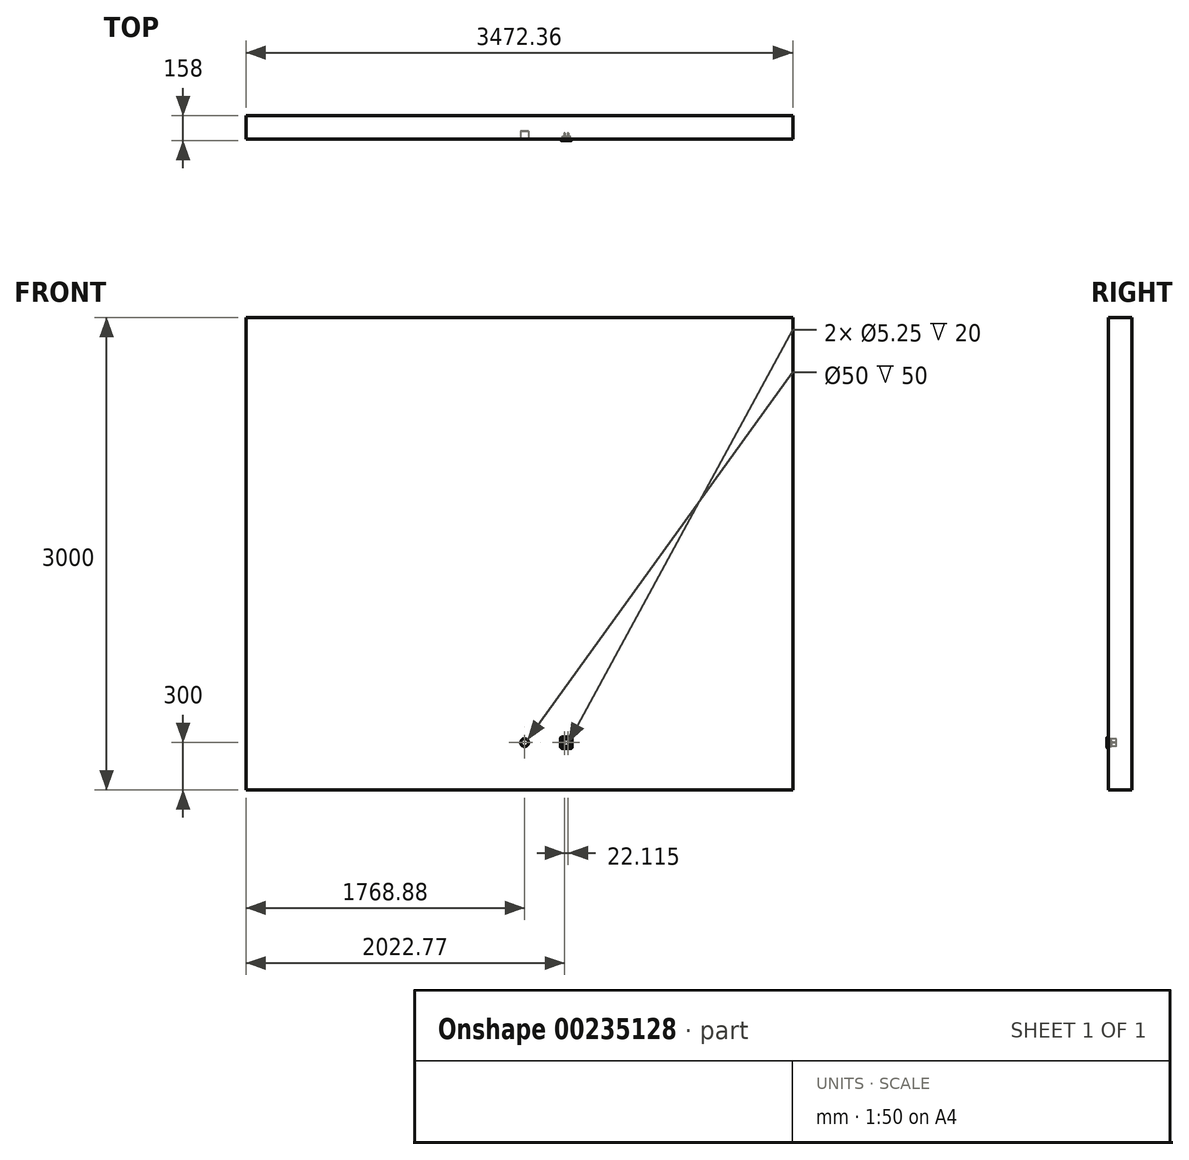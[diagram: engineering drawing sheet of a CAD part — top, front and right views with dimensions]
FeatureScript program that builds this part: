
annotation { "Feature Type Name" : "Feature", "Feature Type Description" : "" }
export const myFeature = defineFeature(function(context is Context, id is Id, definition is map)
    precondition{}
    {
        {
            var Q0;
            Q0=qCreatedBy(makeId("Front.planeOp"),FACE);
            var sketch = newSketch(context, id + "F0", { "sketchPlane" : qUnion([Q0])});
            skLineSegment(sketch, "E0.bottom", {"start": v(0, 0) * mm, "end": v(3472.36, 0) * mm});
            skLineSegment(sketch, "E0.top", {"start": v(0, 3000) * mm, "end": v(3472.36, 3000) * mm});
            skLineSegment(sketch, "E0.left", {"start": v(0, 0) * mm, "end": v(0, 3000) * mm});
            skLineSegment(sketch, "E0.right", {"start": v(3472.36, 0) * mm, "end": v(3472.36, 3000) * mm});
            skSolve(sketch);
        }
        {
            var Q0;
            Q0=makeQuery(id+"F0.imprint","IMPRINT",FACE,{"disambiguationData":[TD([[makeQuery(id+"F0.imprint","IMPRINT",EDGE,{"derivedFrom":sQuery(id+"F0.wireOp",EDGE,"E0.bottom")}),1.0]])]});
            extrude(context, id + "F1", {"entities" : qUnion([Q0]), "depth" : 150 * mm});
        }
        {
            var Q0;
            Q0=makeQuery(id+"F1.opExtrude","CAP_FACE",FACE,{"disambiguationData":[OSD([sQuery(id+"F0.wireOp",EDGE,"E0.bottom"),sQuery(id+"F0.wireOp",EDGE,"E0.top"),sQuery(id+"F0.wireOp",EDGE,"E0.left"),sQuery(id+"F0.wireOp",EDGE,"E0.right")])],"isStart":false});
            var sketch = newSketch(context, id + "F2", { "sketchPlane" : qUnion([Q0])});
            skCircle(sketch, "E1", {"center": v(1768.88, 300) * mm, "radius": 25 * mm});
            skCircle(sketch, "E2", {"center": v(1768.88, 300) * mm, "radius": 24.95 * mm});
            skSolve(sketch);
        }
        {
            var Q0;
            Q0=makeQuery(id+"F2.imprint","IMPRINT",FACE,{"disambiguationData":[TD([[makeQuery(id+"F2.imprint","IMPRINT",EDGE,{"derivedFrom":sQuery(id+"F2.wireOp",EDGE,"E1")}),1.0]])]});
            extrude(context, id + "F3", {"entities" : qUnion([Q0]), "operationType" : NewBodyOperationType.REMOVE, "oppositeDirection" : true, "depth" : 50 * mm});
        }
        {
            var Q0;
            {var subQ0=sQuery(id+"F0.wireOp",EDGE,"E0.right");var subQ1=sQuery(id+"F0.wireOp",EDGE,"E0.left");var subQ2=sQuery(id+"F0.wireOp",EDGE,"E0.top");var subQ3=sQuery(id+"F0.wireOp",EDGE,"E0.bottom");Q0=makeQuery(id+"F3.boolean.opBoolean","SPLIT",FACE,{"disambiguationData":[TD([makeQuery(id+"F1.opExtrude","SWEPT_FACE",FACE,{"disambiguationData":[OSD([subQ3])]})])],"derivedFrom":makeQuery(id+"F1.opExtrude","CAP_FACE",FACE,{"disambiguationData":[OSD([subQ3,subQ2,subQ1,subQ0])],"isStart":false})});}
            var sketch = newSketch(context, id + "F4", { "sketchPlane" : qUnion([Q0])});
            skArc(sketch, "E3", {"start": v(2010.84, 290.18) * mm, "mid": v(2033.83, 275) * mm, "end": v(2056.82, 290.18) * mm});
            skLineSegment(sketch, "E4.bottom", {"start": v(2071.28, 337.45) * mm, "end": v(1996.38, 337.45) * mm});
            skLineSegment(sketch, "E4.top", {"start": v(2071.28, 262.55) * mm, "end": v(1996.38, 262.55) * mm});
            skLineSegment(sketch, "E4.left", {"start": v(2071.28, 337.45) * mm, "end": v(2071.28, 262.55) * mm});
            skLineSegment(sketch, "E4.right", {"start": v(1996.38, 337.45) * mm, "end": v(1996.38, 262.55) * mm});
            skCircle(sketch, "E5", {"center": v(2022.77, 300) * mm, "radius": 2.63 * mm});
            skLineSegment(sketch, "E6", {"start": v(2033.83, 300) * mm, "end": v(2033.83, 328.03) * mm});
            skCircle(sketch, "E7.MirrorC", {"center": v(2044.88, 300) * mm, "radius": 2.63 * mm});
            skLineSegment(sketch, "E8", {"start": v(2010.84, 309.82) * mm, "end": v(2010.84, 302.5) * mm});
            skLineSegment(sketch, "E9", {"start": v(2010.84, 302.5) * mm, "end": v(2008.95, 302.5) * mm});
            skLineSegment(sketch, "E10", {"start": v(2008.95, 302.5) * mm, "end": v(2008.95, 297.5) * mm});
            skLineSegment(sketch, "E11", {"start": v(2008.95, 297.5) * mm, "end": v(2010.84, 297.5) * mm});
            skLineSegment(sketch, "E12", {"start": v(2010.84, 297.5) * mm, "end": v(2010.84, 290.18) * mm});
            skLineSegment(sketch, "E13.MirrorCS", {"start": v(2056.82, 309.82) * mm, "end": v(2056.82, 302.5) * mm});
            skLineSegment(sketch, "E14.MirrorCS", {"start": v(2056.82, 302.5) * mm, "end": v(2058.7, 302.5) * mm});
            skLineSegment(sketch, "E15.MirrorCS", {"start": v(2058.7, 302.5) * mm, "end": v(2058.7, 297.5) * mm});
            skLineSegment(sketch, "E16.MirrorCS", {"start": v(2058.7, 297.5) * mm, "end": v(2056.82, 297.5) * mm});
            skLineSegment(sketch, "E17.MirrorCS", {"start": v(2056.82, 297.5) * mm, "end": v(2056.82, 290.18) * mm});
            skArc(sketch, "E18.trimOffspring", {"start": v(2056.82, 309.82) * mm, "mid": v(2033.83, 325) * mm, "end": v(2010.84, 309.82) * mm});
            skSolve(sketch);
        }
        {
            var Q0;
            Q0 = qSketchRegion(id + "F4", true);
            var Q1;
            Q1=makeQuery(id+"F4.imprint","IMPRINT",FACE,{"disambiguationData":[TD([[makeQuery(id+"F4.imprint","IMPRINT",EDGE,{"derivedFrom":sQuery(id+"F4.wireOp",EDGE,"E4.bottom")}),1.0]])]});
            extrude(context, id + "F5", {"entities" : qUnion([Q0, Q1]), "operationType" : NewBodyOperationType.ADD, "depth" : 8 * mm});
        }
        {
            var Q0;
            Q0=makeQuery(id+"F5.opExtrude","SWEPT_EDGE",EDGE,{"disambiguationData":[OSD([sQuery(id+"F4.wireOp",EDGE,"E4.bottom"),sQuery(id+"F4.wireOp",EDGE,"E4.right")])]});
            var Q1;
            Q1=makeQuery(id+"F5.opExtrude","SWEPT_EDGE",EDGE,{"disambiguationData":[OSD([sQuery(id+"F4.wireOp",EDGE,"E4.top"),sQuery(id+"F4.wireOp",EDGE,"E4.right")])]});
            var Q2;
            Q2=makeQuery(id+"F5.opExtrude","SWEPT_EDGE",EDGE,{"disambiguationData":[OSD([sQuery(id+"F4.wireOp",EDGE,"E4.top"),sQuery(id+"F4.wireOp",EDGE,"E4.left")])]});
            var Q3;
            Q3=makeQuery(id+"F5.opExtrude","SWEPT_EDGE",EDGE,{"disambiguationData":[OSD([sQuery(id+"F4.wireOp",EDGE,"E4.bottom"),sQuery(id+"F4.wireOp",EDGE,"E4.left")])]});
            fillet(context, id + "F6", {"entities" : qUnion([Q0, Q1, Q2, Q3]), "radius" : 13 * mm, "tangentPropagation" : true, "allowEdgeOverflow" : false});
        }
        {
            var Q0;
            {var subQ0=sQuery(id+"F4.wireOp",EDGE,"E4.right");var subQ1=sQuery(id+"F4.wireOp",EDGE,"E4.bottom");Q0=makeQuery(id+"F6.opFillet","BLEND_EDGE",EDGE,{"blendedFrom":[makeQuery(id+"F5.opExtrude","SWEPT_EDGE",EDGE,{"disambiguationData":[OSD([subQ1,subQ0])]}),makeQuery(id+"F5.opExtrude","CAP_FACE",FACE,{"disambiguationData":[OSD([sQuery(id+"F4.wireOp",EDGE,"E3"),subQ1,sQuery(id+"F4.wireOp",EDGE,"E4.top"),sQuery(id+"F4.wireOp",EDGE,"E4.left"),subQ0])],"isStart":false})],"blendedInto":[makeQuery(id+"F5.opExtrude","CAP_FACE",FACE,{"disambiguationData":[OSD([sQuery(id+"F4.wireOp",EDGE,"E3"),subQ1,sQuery(id+"F4.wireOp",EDGE,"E4.top"),sQuery(id+"F4.wireOp",EDGE,"E4.left"),subQ0])],"isStart":false})]});}
            var Q1;
            Q1=makeQuery(id+"F5.opExtrude","CAP_EDGE",EDGE,{"disambiguationData":[OSD([sQuery(id+"F4.wireOp",EDGE,"E4.bottom")])],"isStart":false});
            var Q2;
            {var subQ0=sQuery(id+"F4.wireOp",EDGE,"E4.left");var subQ1=sQuery(id+"F4.wireOp",EDGE,"E4.bottom");Q2=makeQuery(id+"F6.opFillet","BLEND_EDGE",EDGE,{"blendedFrom":[makeQuery(id+"F5.opExtrude","SWEPT_EDGE",EDGE,{"disambiguationData":[OSD([subQ1,subQ0])]}),makeQuery(id+"F5.opExtrude","CAP_FACE",FACE,{"disambiguationData":[OSD([sQuery(id+"F4.wireOp",EDGE,"E3"),subQ1,sQuery(id+"F4.wireOp",EDGE,"E4.top"),subQ0,sQuery(id+"F4.wireOp",EDGE,"E4.right")])],"isStart":false})],"blendedInto":[makeQuery(id+"F5.opExtrude","CAP_FACE",FACE,{"disambiguationData":[OSD([sQuery(id+"F4.wireOp",EDGE,"E3"),subQ1,sQuery(id+"F4.wireOp",EDGE,"E4.top"),subQ0,sQuery(id+"F4.wireOp",EDGE,"E4.right")])],"isStart":false})]});}
            var Q3;
            Q3=makeQuery(id+"F5.opExtrude","CAP_EDGE",EDGE,{"disambiguationData":[OSD([sQuery(id+"F4.wireOp",EDGE,"E4.left")])],"isStart":false});
            var Q4;
            {var subQ0=sQuery(id+"F4.wireOp",EDGE,"E4.left");var subQ1=sQuery(id+"F4.wireOp",EDGE,"E4.top");Q4=makeQuery(id+"F6.opFillet","BLEND_EDGE",EDGE,{"blendedFrom":[makeQuery(id+"F5.opExtrude","SWEPT_EDGE",EDGE,{"disambiguationData":[OSD([subQ1,subQ0])]}),makeQuery(id+"F5.opExtrude","CAP_FACE",FACE,{"disambiguationData":[OSD([sQuery(id+"F4.wireOp",EDGE,"E3"),sQuery(id+"F4.wireOp",EDGE,"E4.bottom"),subQ1,subQ0,sQuery(id+"F4.wireOp",EDGE,"E4.right")])],"isStart":false})],"blendedInto":[makeQuery(id+"F5.opExtrude","CAP_FACE",FACE,{"disambiguationData":[OSD([sQuery(id+"F4.wireOp",EDGE,"E3"),sQuery(id+"F4.wireOp",EDGE,"E4.bottom"),subQ1,subQ0,sQuery(id+"F4.wireOp",EDGE,"E4.right")])],"isStart":false})]});}
            var Q5;
            Q5=makeQuery(id+"F5.opExtrude","CAP_EDGE",EDGE,{"disambiguationData":[OSD([sQuery(id+"F4.wireOp",EDGE,"E4.top")])],"isStart":false});
            var Q6;
            {var subQ0=sQuery(id+"F4.wireOp",EDGE,"E4.right");var subQ1=sQuery(id+"F4.wireOp",EDGE,"E4.top");Q6=makeQuery(id+"F6.opFillet","BLEND_EDGE",EDGE,{"blendedFrom":[makeQuery(id+"F5.opExtrude","SWEPT_EDGE",EDGE,{"disambiguationData":[OSD([subQ1,subQ0])]}),makeQuery(id+"F5.opExtrude","CAP_FACE",FACE,{"disambiguationData":[OSD([sQuery(id+"F4.wireOp",EDGE,"E3"),sQuery(id+"F4.wireOp",EDGE,"E4.bottom"),subQ1,sQuery(id+"F4.wireOp",EDGE,"E4.left"),subQ0])],"isStart":false})],"blendedInto":[makeQuery(id+"F5.opExtrude","CAP_FACE",FACE,{"disambiguationData":[OSD([sQuery(id+"F4.wireOp",EDGE,"E3"),sQuery(id+"F4.wireOp",EDGE,"E4.bottom"),subQ1,sQuery(id+"F4.wireOp",EDGE,"E4.left"),subQ0])],"isStart":false})]});}
            var Q7;
            Q7=makeQuery(id+"F5.opExtrude","CAP_EDGE",EDGE,{"disambiguationData":[OSD([sQuery(id+"F4.wireOp",EDGE,"E4.right")])],"isStart":false});
            fillet(context, id + "F7", {"entities" : qUnion([Q0, Q1, Q2, Q3, Q4, Q5, Q6, Q7]), "radius" : 6.76 * mm, "tangentPropagation" : true, "rho" : 0.3, "crossSection" : FilletCrossSection.CONIC, "allowEdgeOverflow" : false});
        }
        {
            var Q0;
            Q0=makeQuery(id+"F4.imprint","IMPRINT",FACE,{"disambiguationData":[TD([[makeQuery(id+"F4.imprint","IMPRINT",EDGE,{"derivedFrom":sQuery(id+"F4.wireOp",EDGE,"E3")}),1.0]])]});
            extrude(context, id + "F8", {"entities" : qUnion([Q0]), "operationType" : NewBodyOperationType.REMOVE, "oppositeDirection" : true, "depth" : 20 * mm});
        }
        {
            var Q0;
            {var subQ0=sQuery(id+"F0.wireOp",EDGE,"E0.right");var subQ1=sQuery(id+"F0.wireOp",EDGE,"E0.left");var subQ2=sQuery(id+"F0.wireOp",EDGE,"E0.top");var subQ3=sQuery(id+"F0.wireOp",EDGE,"E0.bottom");Q0=makeQuery(id+"F8.boolean.opBoolean","SPLIT",FACE,{"disambiguationData":[TD([makeQuery(id+"F8.opExtrude","SWEPT_FACE",FACE,{"disambiguationData":[OSD([sQuery(id+"F4.wireOp",EDGE,"E5")])]})])],"derivedFrom":makeQuery(id+"F5.boolean.opBoolean","SPLIT",FACE,{"disambiguationData":[TD([makeQuery(id+"F5.opExtrude","SWEPT_FACE",FACE,{"disambiguationData":[OSD([sQuery(id+"F4.wireOp",EDGE,"E3")])]})])],"derivedFrom":makeQuery(id+"F3.boolean.opBoolean","SPLIT",FACE,{"disambiguationData":[TD([makeQuery(id+"F1.opExtrude","SWEPT_FACE",FACE,{"disambiguationData":[OSD([subQ3])]})])],"derivedFrom":makeQuery(id+"F1.opExtrude","CAP_FACE",FACE,{"disambiguationData":[OSD([subQ3,subQ2,subQ1,subQ0])],"isStart":false})})})});}
            var Q1;
            {var subQ0=sQuery(id+"F0.wireOp",EDGE,"E0.right");var subQ1=sQuery(id+"F0.wireOp",EDGE,"E0.left");var subQ2=sQuery(id+"F0.wireOp",EDGE,"E0.top");var subQ3=sQuery(id+"F0.wireOp",EDGE,"E0.bottom");Q1=makeQuery(id+"F8.boolean.opBoolean","SPLIT",FACE,{"disambiguationData":[TD([makeQuery(id+"F8.opExtrude","SWEPT_FACE",FACE,{"disambiguationData":[OSD([sQuery(id+"F4.wireOp",EDGE,"E7.MirrorC")])]})])],"derivedFrom":makeQuery(id+"F5.boolean.opBoolean","SPLIT",FACE,{"disambiguationData":[TD([makeQuery(id+"F5.opExtrude","SWEPT_FACE",FACE,{"disambiguationData":[OSD([sQuery(id+"F4.wireOp",EDGE,"E3")])]})])],"derivedFrom":makeQuery(id+"F3.boolean.opBoolean","SPLIT",FACE,{"disambiguationData":[TD([makeQuery(id+"F1.opExtrude","SWEPT_FACE",FACE,{"disambiguationData":[OSD([subQ3])]})])],"derivedFrom":makeQuery(id+"F1.opExtrude","CAP_FACE",FACE,{"disambiguationData":[OSD([subQ3,subQ2,subQ1,subQ0])],"isStart":false})})})});}
            extrude(context, id + "F9", {"entities" : qUnion([Q0, Q1]), "operationType" : NewBodyOperationType.REMOVE, "oppositeDirection" : true, "depth" : 40 * mm});
        }
    });
